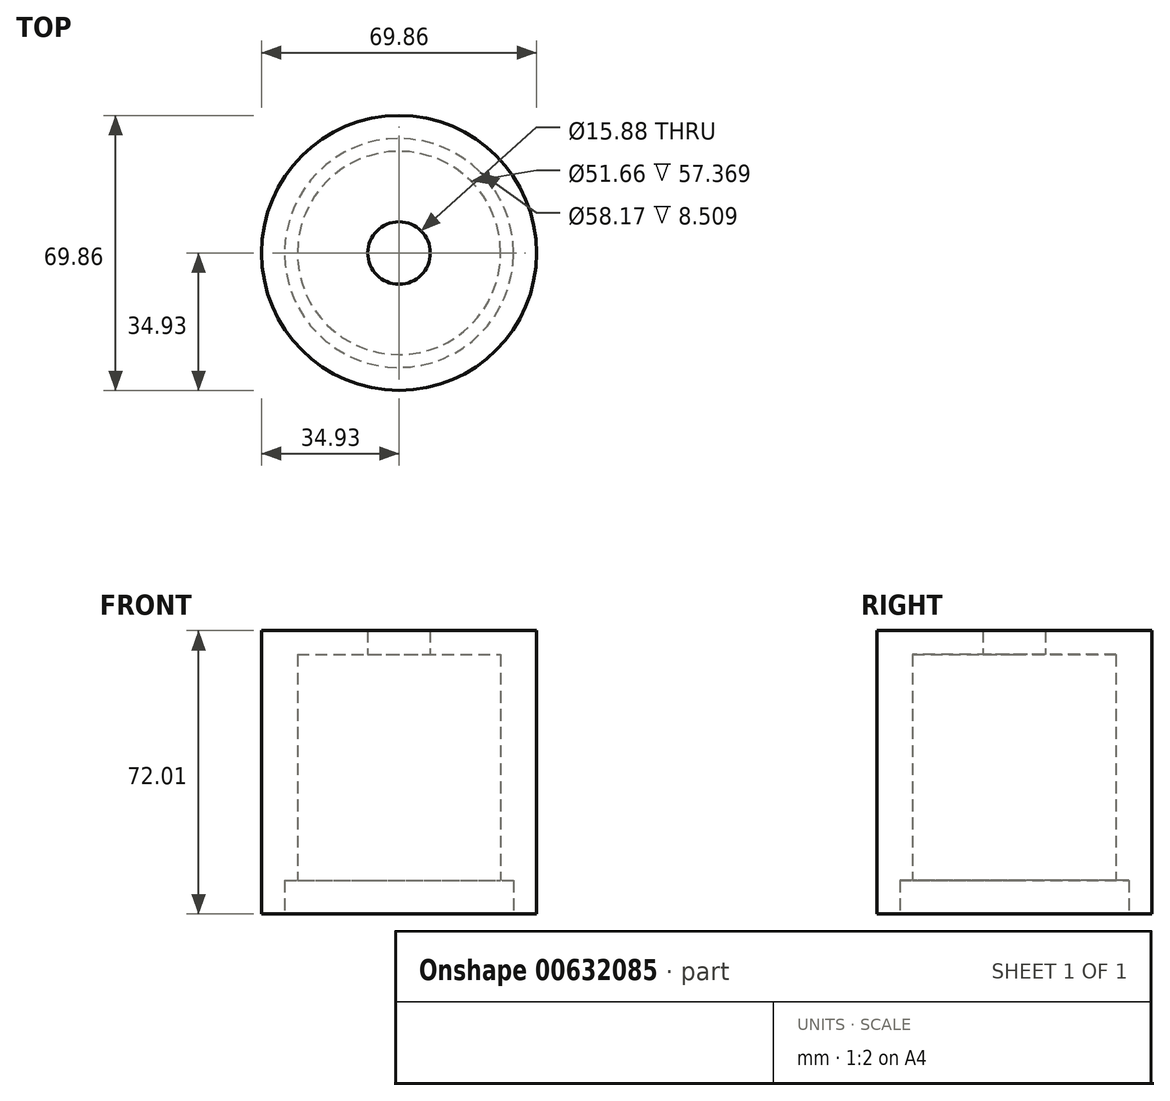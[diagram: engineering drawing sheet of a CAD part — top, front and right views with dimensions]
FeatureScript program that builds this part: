
annotation { "Feature Type Name" : "Feature", "Feature Type Description" : "" }
export const myFeature = defineFeature(function(context is Context, id is Id, definition is map)
    precondition{}
    {
        {
            var Q0;
            Q0=qCreatedBy(makeId("Front.planeOp"),FACE);
            var sketch = newSketch(context, id + "F0", { "sketchPlane" : qUnion([Q0])});
            skLineSegment(sketch, "E0", {"start": v(34.92, 0) * mm, "end": v(34.92, 63.5) * mm});
            skLineSegment(sketch, "E1", {"start": v(34.92, 0) * mm, "end": v(34.92, -8.5) * mm});
            skLineSegment(sketch, "E2", {"start": v(34.92, -8.5) * mm, "end": v(29.08, -8.5) * mm});
            skLineSegment(sketch, "E3", {"start": v(29.08, -8.5) * mm, "end": v(29.08, 0) * mm});
            skLineSegment(sketch, "E4", {"start": v(29.08, 0) * mm, "end": v(25.83, 0) * mm});
            skLineSegment(sketch, "E5", {"start": v(25.83, 0) * mm, "end": v(25.83, 57.37) * mm});
            skLineSegment(sketch, "E6", {"start": v(34.92, 63.5) * mm, "end": v(7.94, 63.5) * mm});
            skPoint(sketch, "E7.orphan", {"position": v(25.83, 62.25) * mm});
            skLineSegment(sketch, "E8", {"start": v(25.83, 57.37) * mm, "end": v(7.94, 57.37) * mm});
            skLineSegment(sketch, "E9", {"start": v(7.94, 57.37) * mm, "end": v(7.94, 63.5) * mm});
            skPoint(sketch, "E10.orphan", {"position": v(25.83, 63.5) * mm});
            skPoint(sketch, "E11.orphan", {"position": v(7.94, 68.81) * mm});
            skLineSegment(sketch, "E12", {"start": v(0, 0) * mm, "end": v(0, 72.78) * mm});
            skSolve(sketch);
        }
        {
            var Q0;
            Q0 = qSketchRegion(id + "F0", true);
            var Q1;
            Q1=sQuery(id+"F0.wireOp",EDGE,"E12");
            revolve(context, id + "F1", {"entities" : qUnion([Q0]), "axis" : qUnion([Q1]), "revolveType" : RevolveType.FULL});
        }
    });
